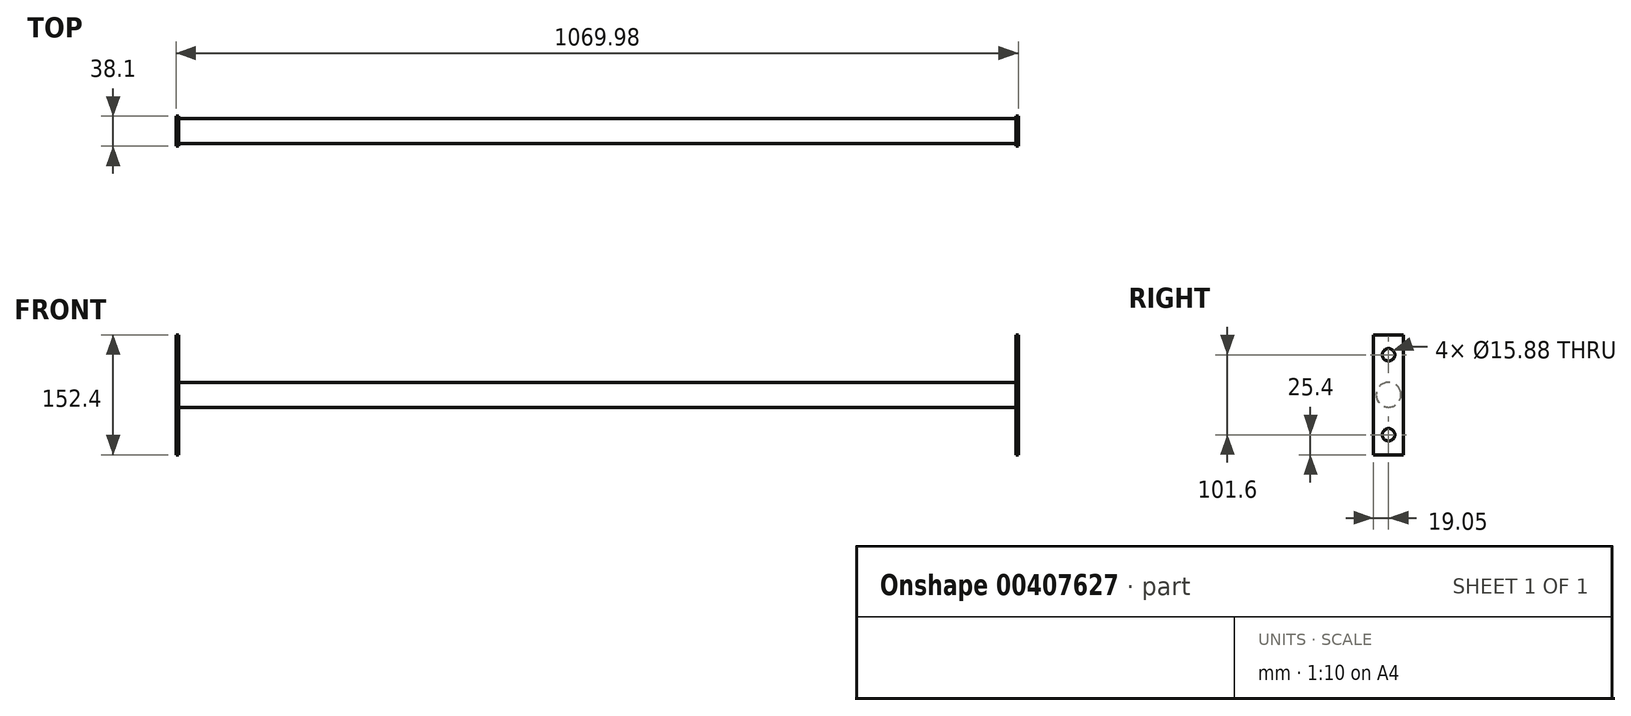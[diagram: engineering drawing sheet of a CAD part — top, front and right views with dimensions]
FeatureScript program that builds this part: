
annotation { "Feature Type Name" : "Feature", "Feature Type Description" : "" }
export const myFeature = defineFeature(function(context is Context, id is Id, definition is map)
    precondition{}
    {
        {
            var Q0;
            Q0=qCreatedBy(makeId("Right.planeOp"),FACE);
            var sketch = newSketch(context, id + "F0", { "sketchPlane" : qUnion([Q0])});
            skCircle(sketch, "E0", {"center": v(0, 0) * mm, "radius": 15.88 * mm});
            skSolve(sketch);
        }
        {
            var Q0;
            Q0 = qSketchRegion(id + "F0", true);
            extrude(context, id + "F1", {"entities" : qUnion([Q0]), "depth" : 1069.97 * mm});
        }
        {
            var Q0;
            Q0=qCreatedBy(makeId("Right.planeOp"),FACE);
            var sketch = newSketch(context, id + "F2", { "sketchPlane" : qUnion([Q0])});
            skLineSegment(sketch, "E1.bottom", {"start": v(19.05, 76.2) * mm, "end": v(-19.05, 76.2) * mm});
            skLineSegment(sketch, "E1.top", {"start": v(19.05, -76.2) * mm, "end": v(-19.05, -76.2) * mm});
            skLineSegment(sketch, "E1.left", {"start": v(19.05, 76.2) * mm, "end": v(19.05, -76.2) * mm});
            skLineSegment(sketch, "E1.right", {"start": v(-19.05, 76.2) * mm, "end": v(-19.05, -76.2) * mm});
            skSolve(sketch);
        }
        {
            var Q0;
            Q0 = qSketchRegion(id + "F2", true);
            extrude(context, id + "F3", {"entities" : qUnion([Q0]), "operationType" : NewBodyOperationType.ADD, "depth" : 3.17 * mm, "offsetDistance" : 25.4 * mm});
        }
        {
            var Q0;
            Q0=makeQuery(id+"F3.boolean.opBoolean","MERGE",FACE,{"derivedFrom":[makeQuery(id+"F1.opExtrude","CAP_FACE",FACE,{"disambiguationData":[OSD([sQuery(id+"F0.wireOp",EDGE,"E0")])],"isStart":true}),makeQuery(id+"F3.opExtrude","CAP_FACE",FACE,{"disambiguationData":[OSD([sQuery(id+"F2.wireOp",EDGE,"E1.bottom"),sQuery(id+"F2.wireOp",EDGE,"E1.top"),sQuery(id+"F2.wireOp",EDGE,"E1.left"),sQuery(id+"F2.wireOp",EDGE,"E1.right")])],"isStart":true})]});
            var sketch = newSketch(context, id + "F4", { "sketchPlane" : qUnion([Q0])});
            skPoint(sketch, "E2", {"position": v(0, -50.8) * mm});
            skPoint(sketch, "E3", {"position": v(0, 50.8) * mm});
            skSolve(sketch);
        }
        {
            var Q0;
            Q0=sQuery(id+"F4.wireOp",VERTEX,"E3");
            var Q1;
            Q1=sQuery(id+"F4.wireOp",VERTEX,"E2");
            var Q2;
            Q2=makeQuery(id+"F1.opExtrude","SWEPT_BODY",BODY,{"disambiguationData":[OSD([sQuery(id+"F0.wireOp",EDGE,"E0")])]});
            hole(context, id + "F5", {"style" : HoleStyle.SIMPLE, "endStyle" : HoleEndStyle.THROUGH, "holeDiameter" : 15.88 * mm, "majorDiameter" : 6.35 * mm, "isTappedThrough" : true, "tappedDepth" : 12.7 * mm, "tapClearance" : 3, "locations" : qUnion([Q0, Q1]), "scope" : qUnion([Q2]), "startStyle" : HoleStartStyle.PART});
        }
        {
            var Q0;
            Q0=makeQuery(id+"F1.opExtrude","CAP_FACE",FACE,{"disambiguationData":[OSD([sQuery(id+"F0.wireOp",EDGE,"E0")])],"isStart":false});
            var sketch = newSketch(context, id + "F6", { "sketchPlane" : qUnion([Q0])});
            skLineSegment(sketch, "E4.0", {"start": v(-19.05, 76.2) * mm, "end": v(-19.05, -76.2) * mm});
            skLineSegment(sketch, "E5.0", {"start": v(19.05, 76.2) * mm, "end": v(19.05, -76.2) * mm});
            skLineSegment(sketch, "E6.0", {"start": v(19.05, -76.2) * mm, "end": v(-19.05, -76.2) * mm});
            skLineSegment(sketch, "E7.0", {"start": v(19.05, 76.2) * mm, "end": v(-19.05, 76.2) * mm});
            skSolve(sketch);
        }
        {
            var Q0;
            Q0 = qSketchRegion(id + "F6", true);
            extrude(context, id + "F7", {"entities" : qUnion([Q0]), "operationType" : NewBodyOperationType.ADD, "oppositeDirection" : true, "depth" : 3.17 * mm, "offsetDistance" : 25.4 * mm});
        }
        {
            var Q0;
            Q0=makeQuery(id+"F7.boolean.opBoolean","MERGE",FACE,{"derivedFrom":[makeQuery(id+"F1.opExtrude","CAP_FACE",FACE,{"disambiguationData":[OSD([sQuery(id+"F0.wireOp",EDGE,"E0")])],"isStart":false}),makeQuery(id+"F7.opExtrude","CAP_FACE",FACE,{"disambiguationData":[OSD([sQuery(id+"F6.wireOp",EDGE,"E4.0"),sQuery(id+"F6.wireOp",EDGE,"E5.0"),sQuery(id+"F6.wireOp",EDGE,"E6.0"),sQuery(id+"F6.wireOp",EDGE,"E7.0")])],"isStart":true})]});
            var sketch = newSketch(context, id + "F8", { "sketchPlane" : qUnion([Q0])});
            skPoint(sketch, "E8", {"position": v(0, 50.8) * mm});
            skPoint(sketch, "E9", {"position": v(0, -50.8) * mm});
            skSolve(sketch);
        }
        {
            var Q0;
            Q0=sQuery(id+"F8.wireOp",VERTEX,"E8");
            var Q1;
            Q1=sQuery(id+"F8.wireOp",VERTEX,"E9");
            var Q2;
            Q2=makeQuery(id+"F1.opExtrude","SWEPT_BODY",BODY,{"disambiguationData":[OSD([sQuery(id+"F0.wireOp",EDGE,"E0")])]});
            hole(context, id + "F9", {"style" : HoleStyle.SIMPLE, "endStyle" : HoleEndStyle.THROUGH, "holeDiameter" : 15.88 * mm, "majorDiameter" : 6.35 * mm, "isTappedThrough" : true, "tappedDepth" : 12.7 * mm, "tapClearance" : 3, "locations" : qUnion([Q0, Q1]), "scope" : qUnion([Q2]), "startStyle" : HoleStartStyle.PART});
        }
    });
